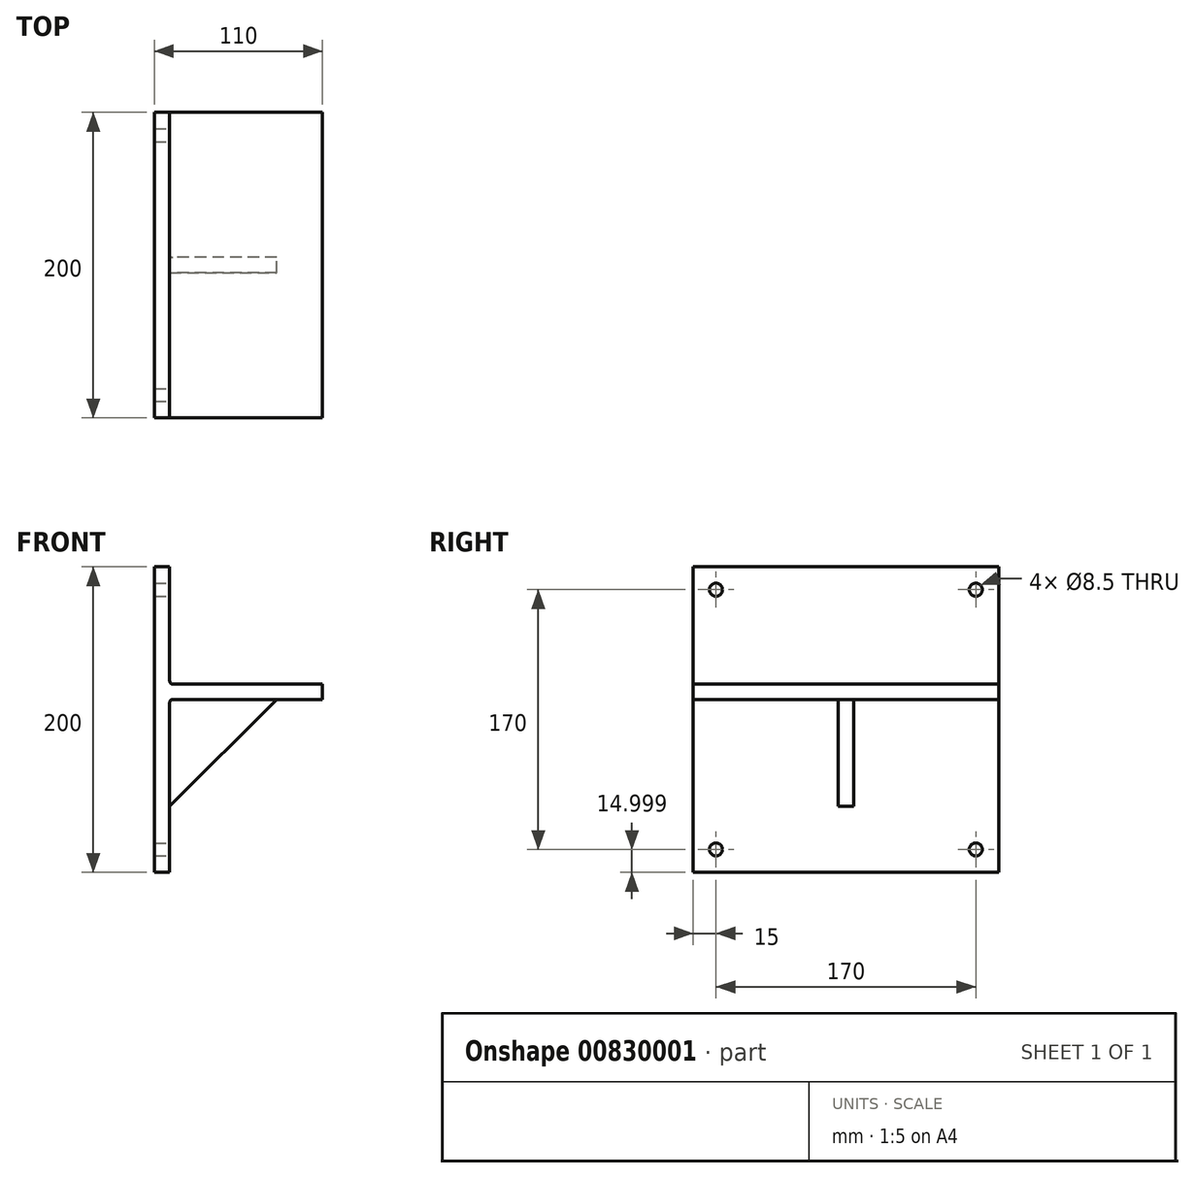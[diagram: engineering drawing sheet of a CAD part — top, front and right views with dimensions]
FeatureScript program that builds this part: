
annotation { "Feature Type Name" : "Feature", "Feature Type Description" : "" }
export const myFeature = defineFeature(function(context is Context, id is Id, definition is map)
    precondition{}
    {
        {
            var Q0;
            Q0=qCreatedBy(makeId("Front.planeOp"),FACE);
            var sketch = newSketch(context, id + "F0", { "sketchPlane" : qUnion([Q0])});
            skLineSegment(sketch, "E0.bottom", {"start": v(-64.73, 91.2) * mm, "end": v(-54.73, 91.2) * mm});
            skLineSegment(sketch, "E0.top", {"start": v(-64.73, -108.8) * mm, "end": v(-54.73, -108.8) * mm});
            skLineSegment(sketch, "E0.left", {"start": v(-64.73, 91.2) * mm, "end": v(-64.73, -108.8) * mm});
            skLineSegment(sketch, "E0.right", {"start": v(-54.73, 91.2) * mm, "end": v(-54.73, -108.8) * mm});
            skLineSegment(sketch, "E1.bottom", {"start": v(-54.73, 14.4) * mm, "end": v(45.27, 14.4) * mm});
            skLineSegment(sketch, "E1.top", {"start": v(-54.73, 4.4) * mm, "end": v(45.27, 4.4) * mm});
            skLineSegment(sketch, "E1.left", {"start": v(-54.73, 14.4) * mm, "end": v(-54.73, 4.4) * mm});
            skLineSegment(sketch, "E1.right", {"start": v(45.27, 14.4) * mm, "end": v(45.27, 4.4) * mm});
            skSolve(sketch);
        }
        {
            var Q0;
            Q0 = qSketchRegion(id + "F0", true);
            var Q1;
            {var subQ1=sQuery(id+"F0.wireOp",EDGE,"E0.bottom");Q1=makeQuery(id+"F0.imprint","IMPRINT",FACE,{"disambiguationData":[TD([[makeQuery(id+"F0.imprint","IMPRINT",EDGE,{"derivedFrom":subQ1}),-1.0]])]});}
            extrude(context, id + "F1", {"entities" : qUnion([Q0, Q1]), "depth" : 200 * mm, "offsetDistance" : 25 * mm});
        }
        {
            var Q0;
            {var subQ0=sQuery(id+"F0.wireOp",EDGE,"E0.right");Q0=makeQuery(id+"F1.opExtrude","SWEPT_FACE",FACE,{"disambiguationData":[OSD([subQ0]),TDD([makeQuery(id+"F0.imprint","IMPRINT",EDGE,{"disambiguationData":[TD([[makeQuery(id+"F0.imprint","INTERSECT",VERTEX,{"derivedFrom":[sQuery(id+"F0.wireOp",EDGE,"E0.top"),subQ0]}),1.0]])],"derivedFrom":subQ0})])]});}
            var sketch = newSketch(context, id + "F2", { "sketchPlane" : qUnion([Q0])});
            skLineSegment(sketch, "E2.bottom", {"start": v(-105, 4.4) * mm, "end": v(-95, 4.4) * mm});
            skLineSegment(sketch, "E2.top", {"start": v(-105, -65.6) * mm, "end": v(-95, -65.6) * mm});
            skLineSegment(sketch, "E2.left", {"start": v(-105, 4.4) * mm, "end": v(-105, -65.6) * mm});
            skLineSegment(sketch, "E2.right", {"start": v(-95, 4.4) * mm, "end": v(-95, -65.6) * mm});
            skSolve(sketch);
        }
        {
            var Q0;
            Q0 = qSketchRegion(id + "F2", true);
            var Q1;
            Q1=makeQuery(id+"F2.imprint","IMPRINT",FACE,{"disambiguationData":[TD([[makeQuery(id+"F2.imprint","IMPRINT",EDGE,{"derivedFrom":sQuery(id+"F2.wireOp",EDGE,"E2.bottom")}),-1.0]])]});
            extrude(context, id + "F3", {"entities" : qUnion([Q0, Q1]), "operationType" : NewBodyOperationType.ADD, "depth" : 70 * mm, "offsetDistance" : 25 * mm});
        }
        {
            var Q0;
            Q0=makeQuery(id+"F3.opExtrude","SWEPT_FACE",FACE,{"disambiguationData":[OSD([sQuery(id+"F2.wireOp",EDGE,"E2.left")])]});
            var sketch = newSketch(context, id + "F4", { "sketchPlane" : qUnion([Q0])});
            skLineSegment(sketch, "E3", {"start": v(-54.73, -65.6) * mm, "end": v(15.27, 4.4) * mm});
            skSolve(sketch);
        }
        {
            var Q0;
            Q0=makeQuery(id+"F4.imprint","IMPRINT",FACE,{"disambiguationData":[TD([[makeQuery(id+"F4.imprint","IMPRINT",EDGE,{"derivedFrom":sQuery(id+"F4.wireOp",EDGE,"E3")}),-1.0]])]});
            extrude(context, id + "F5", {"entities" : qUnion([Q0]), "operationType" : NewBodyOperationType.REMOVE, "oppositeDirection" : true, "depth" : 25 * mm, "offsetDistance" : 25 * mm});
        }
        {
            var Q0;
            {var subQ0=sQuery(id+"F0.wireOp",EDGE,"E0.right");Q0=makeQuery(id+"F1.opExtrude","SWEPT_FACE",FACE,{"disambiguationData":[OSD([subQ0]),TDD([makeQuery(id+"F0.imprint","IMPRINT",EDGE,{"disambiguationData":[TD([[makeQuery(id+"F0.imprint","INTERSECT",VERTEX,{"derivedFrom":[sQuery(id+"F0.wireOp",EDGE,"E0.bottom"),subQ0]}),-1.0]])],"derivedFrom":subQ0})])]});}
            var sketch = newSketch(context, id + "F6", { "sketchPlane" : qUnion([Q0])});
            skPoint(sketch, "E4", {"position": v(-185, 76.2) * mm});
            skPoint(sketch, "E5", {"position": v(-15, 76.2) * mm});
            skPoint(sketch, "E6", {"position": v(-185, -93.8) * mm});
            skPoint(sketch, "E7", {"position": v(-15, -93.8) * mm});
            skCircle(sketch, "E8", {"center": v(-185, 76.2) * mm, "radius": 4.25 * mm});
            skCircle(sketch, "E9", {"center": v(-15, 76.2) * mm, "radius": 4.25 * mm});
            skCircle(sketch, "E10", {"center": v(-185, -93.8) * mm, "radius": 4.25 * mm});
            skCircle(sketch, "E11", {"center": v(-15, -93.8) * mm, "radius": 4.25 * mm});
            skSolve(sketch);
        }
        {
            var Q0;
            Q0=makeQuery(id+"F6.imprint","IMPRINT",FACE,{"disambiguationData":[TD([[makeQuery(id+"F6.imprint","IMPRINT",EDGE,{"derivedFrom":sQuery(id+"F6.wireOp",EDGE,"E9")}),1.0]])]});
            var Q1;
            Q1=sQuery(id+"F6.wireOp",EDGE,"E10");
            var Q2;
            Q2=sQuery(id+"F6.wireOp",EDGE,"E11");
            var Q3;
            Q3=sQuery(id+"F6.wireOp",EDGE,"E9");
            var Q4;
            Q4=sQuery(id+"F6.wireOp",EDGE,"E8");
            extrude(context, id + "F7", {"entities" : qUnion([Q0]), "operationType" : NewBodyOperationType.REMOVE, "surfaceEntities" : qUnion([Q1, Q2, Q3, Q4]), "oppositeDirection" : true, "depth" : 25 * mm, "offsetDistance" : 25 * mm});
        }
        {
            var Q0;
            Q0 = qSketchRegion(id + "F6", true);
            extrude(context, id + "F8", {"entities" : qUnion([Q0]), "operationType" : NewBodyOperationType.REMOVE, "oppositeDirection" : true, "depth" : 25 * mm, "offsetDistance" : 25 * mm});
        }
        {
            var Q0;
            Q0=makeQuery(id+"F1.opExtrude","SWEPT_EDGE",EDGE,{"disambiguationData":[OSD([sQuery(id+"F0.wireOp",EDGE,"E0.right"),sQuery(id+"F0.wireOp",EDGE,"E1.bottom"),sQuery(id+"F0.wireOp",EDGE,"E1.left")])]});
            var Q1;
            {var subQ0=sQuery(id+"F0.wireOp",EDGE,"E1.top");var subQ1=sQuery(id+"F0.wireOp",EDGE,"E0.right");var subQ3=sQuery(id+"F0.wireOp",EDGE,"E1.left");Q1=makeQuery(id+"F3.boolean.opBoolean","SPLIT",EDGE,{"disambiguationData":[TD([makeQuery(id+"F3.opExtrude","SWEPT_FACE",FACE,{"disambiguationData":[OSD([sQuery(id+"F2.wireOp",EDGE,"E2.left")])]})])],"derivedFrom":makeQuery(id+"F1.opExtrude","SWEPT_EDGE",EDGE,{"disambiguationData":[OSD([subQ1,subQ0,subQ3])]})});}
            var Q2;
            {var subQ0=sQuery(id+"F0.wireOp",EDGE,"E1.top");var subQ1=sQuery(id+"F0.wireOp",EDGE,"E0.right");var subQ3=sQuery(id+"F0.wireOp",EDGE,"E1.left");Q2=makeQuery(id+"F3.boolean.opBoolean","SPLIT",EDGE,{"disambiguationData":[TD([makeQuery(id+"F3.opExtrude","SWEPT_FACE",FACE,{"disambiguationData":[OSD([sQuery(id+"F2.wireOp",EDGE,"E2.right")])]})])],"derivedFrom":makeQuery(id+"F1.opExtrude","SWEPT_EDGE",EDGE,{"disambiguationData":[OSD([subQ1,subQ0,subQ3])]})});}
            var Q3;
            Q3=makeQuery(id+"F3.opExtrude","CAP_EDGE",EDGE,{"disambiguationData":[OSD([sQuery(id+"F2.wireOp",EDGE,"E2.right")])],"isStart":true});
            var Q4;
            Q4=makeQuery(id+"F3.opExtrude","CAP_EDGE",EDGE,{"disambiguationData":[OSD([sQuery(id+"F2.wireOp",EDGE,"E2.left")])],"isStart":true});
            var Q5;
            {var subQ0=sQuery(id+"F2.wireOp",EDGE,"E2.top");Q5=makeQuery(id+"F5.boolean.opBoolean","MERGE",EDGE,{"derivedFrom":[makeQuery(id+"F3.opExtrude","CAP_EDGE",EDGE,{"disambiguationData":[OSD([subQ0])],"isStart":true}),makeQuery(id+"F5.opExtrude","SWEPT_EDGE",EDGE,{"disambiguationData":[OSD([subQ0,sQuery(id+"F2.wireOp",EDGE,"E2.left"),sQuery(id+"F4.wireOp",EDGE,"E3")])]})]});}
            var Q6;
            Q6=makeQuery(id+"F3.opExtrude","SWEPT_EDGE",EDGE,{"disambiguationData":[OSD([sQuery(id+"F0.wireOp",EDGE,"E0.right"),sQuery(id+"F0.wireOp",EDGE,"E1.top"),sQuery(id+"F0.wireOp",EDGE,"E1.left"),sQuery(id+"F2.wireOp",EDGE,"E2.bottom"),sQuery(id+"F2.wireOp",EDGE,"E2.left")])]});
            var Q7;
            {var subQ0=sQuery(id+"F2.wireOp",EDGE,"E2.bottom");Q7=makeQuery(id+"F5.boolean.opBoolean","MERGE",EDGE,{"derivedFrom":[makeQuery(id+"F3.opExtrude","CAP_EDGE",EDGE,{"disambiguationData":[OSD([subQ0])],"isStart":false}),makeQuery(id+"F5.opExtrude","SWEPT_EDGE",EDGE,{"disambiguationData":[OSD([sQuery(id+"F0.wireOp",EDGE,"E0.right"),sQuery(id+"F0.wireOp",EDGE,"E1.top"),sQuery(id+"F0.wireOp",EDGE,"E1.left"),subQ0,sQuery(id+"F2.wireOp",EDGE,"E2.left"),sQuery(id+"F4.wireOp",EDGE,"E3")])]})]});}
            var Q8;
            Q8=makeQuery(id+"F3.opExtrude","SWEPT_EDGE",EDGE,{"disambiguationData":[OSD([sQuery(id+"F0.wireOp",EDGE,"E0.right"),sQuery(id+"F0.wireOp",EDGE,"E1.top"),sQuery(id+"F0.wireOp",EDGE,"E1.left"),sQuery(id+"F2.wireOp",EDGE,"E2.bottom"),sQuery(id+"F2.wireOp",EDGE,"E2.right")])]});
            fillet(context, id + "F9", {"entities" : qUnion([Q0, Q1, Q2, Q3, Q4, Q5, Q6, Q7, Q8]), "radius" : 2 * mm, "tangentPropagation" : true, "allowEdgeOverflow" : false});
        }
    });
